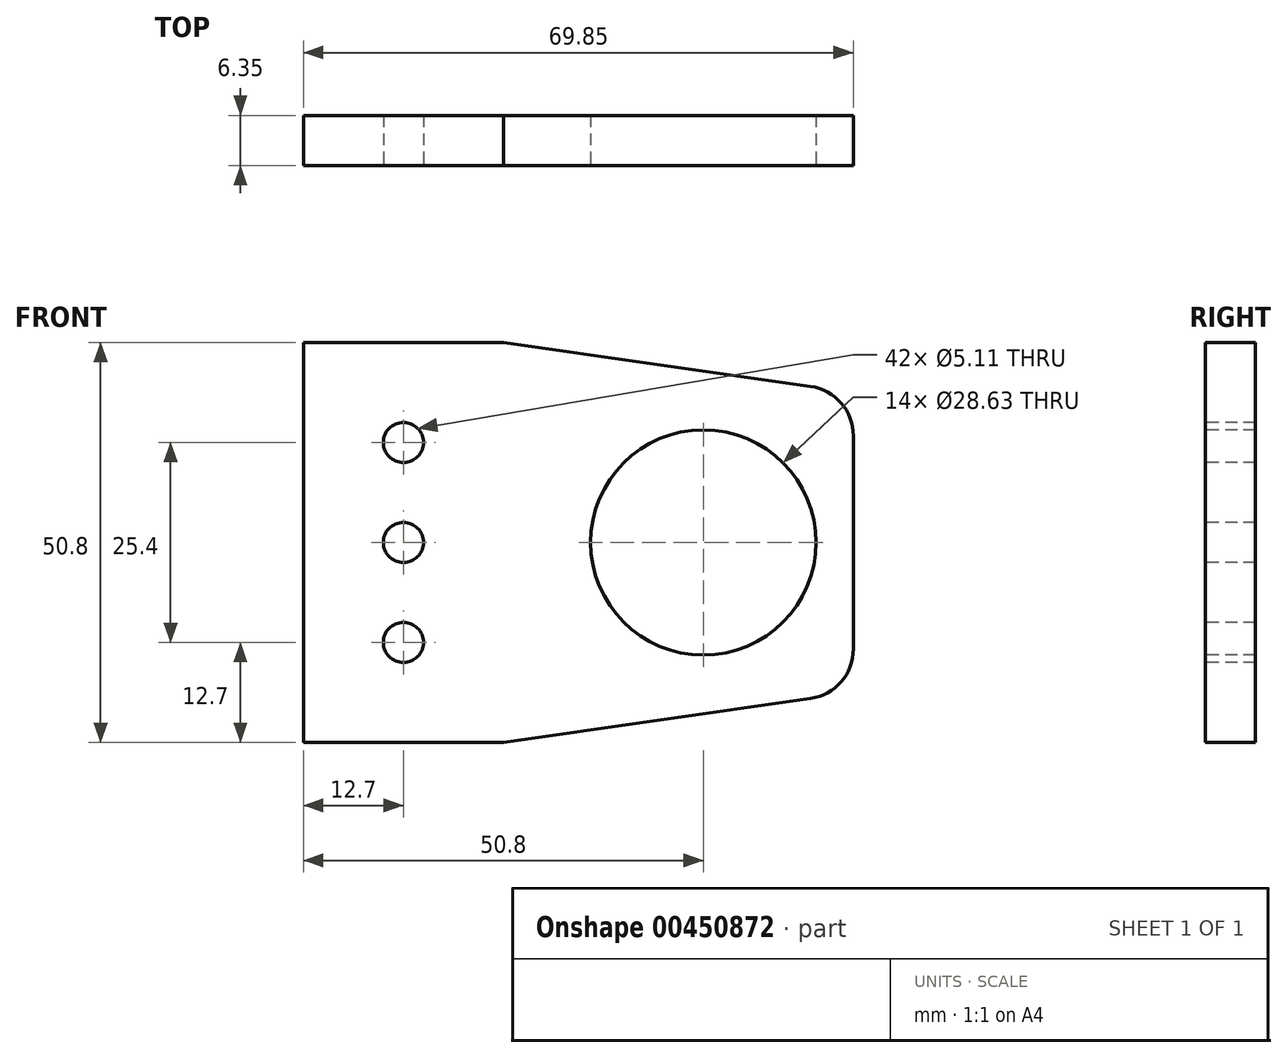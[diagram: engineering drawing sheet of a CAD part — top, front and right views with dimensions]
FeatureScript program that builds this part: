
annotation { "Feature Type Name" : "Feature", "Feature Type Description" : "" }
export const myFeature = defineFeature(function(context is Context, id is Id, definition is map)
    precondition{}
    {
        {
            var Q0;
            Q0=qCreatedBy(makeId("Front.planeOp"),FACE);
            var sketch = newSketch(context, id + "F0", { "sketchPlane" : qUnion([Q0])});
            skLineSegment(sketch, "E0.bottom", {"start": v(0, 25.4) * mm, "end": v(-25.4, 25.4) * mm});
            skLineSegment(sketch, "E0.top", {"start": v(0, -25.4) * mm, "end": v(-25.4, -25.4) * mm});
            skLineSegment(sketch, "E0.left", {"start": v(0, 25.4) * mm, "end": v(0, -25.4) * mm});
            skLineSegment(sketch, "E0.right", {"start": v(-25.4, 25.4) * mm, "end": v(-25.4, -25.4) * mm});
            skLineSegment(sketch, "E1", {"start": v(0, 0) * mm, "end": v(44.45, 0) * mm, "construction": true});
            skLineSegment(sketch, "E2", {"start": v(0, -25.4) * mm, "end": v(39, -19.83) * mm});
            skLineSegment(sketch, "E3", {"start": v(44.45, -13.54) * mm, "end": v(44.45, 0) * mm});
            skLineSegment(sketch, "E4.MirrorCS", {"start": v(0, 25.4) * mm, "end": v(39, 19.83) * mm});
            skLineSegment(sketch, "E5.MirrorCS", {"start": v(44.45, 13.54) * mm, "end": v(44.45, 0) * mm});
            skPoint(sketch, "E6.visualSharp", {"position": v(44.45, -19.05) * mm});
            skArc(sketch, "E6.filletArc", {"start": v(39, -19.83) * mm, "mid": v(42.9, -17.7) * mm, "end": v(44.45, -13.54) * mm});
            skPoint(sketch, "E7.visualSharp", {"position": v(44.45, 19.05) * mm});
            skArc(sketch, "E7.filletArc", {"start": v(44.45, 13.54) * mm, "mid": v(42.9, 17.7) * mm, "end": v(39, 19.83) * mm});
            skSolve(sketch);
        }
        {
            var Q0;
            Q0=qSketchRegion(id+"F0",true);
            extrude(context, id + "F1", {"entities" : qUnion([Q0]), "depth" : 6.35 * mm});
        }
        {
            var Q0;
            Q0=makeQuery(id+"F1.opExtrude","CAP_FACE",FACE,{"disambiguationData":[OSD([sQuery(id+"F0.wireOp",EDGE,"E0.bottom"),sQuery(id+"F0.wireOp",EDGE,"E0.top"),sQuery(id+"F0.wireOp",EDGE,"E0.right"),sQuery(id+"F0.wireOp",EDGE,"E2"),sQuery(id+"F0.wireOp",EDGE,"E3"),sQuery(id+"F0.wireOp",EDGE,"E4.MirrorCS"),sQuery(id+"F0.wireOp",EDGE,"E5.MirrorCS"),sQuery(id+"F0.wireOp",EDGE,"E6.filletArc"),sQuery(id+"F0.wireOp",EDGE,"E7.filletArc")])],"isStart":false});
            var sketch = newSketch(context, id + "F2", { "sketchPlane" : qUnion([Q0])});
            skLineSegment(sketch, "E8", {"start": v(-12.7, 25.4) * mm, "end": v(-12.7, -25.4) * mm, "construction": true});
            skPoint(sketch, "E9", {"position": v(-12.7, 12.7) * mm});
            skPoint(sketch, "E10", {"position": v(-12.7, 0) * mm});
            skPoint(sketch, "E11", {"position": v(-12.7, -12.7) * mm});
            skSolve(sketch);
        }
        {
            var Q0;
            Q0=sQuery(id+"F2.wireOp",VERTEX,"E9");
            var Q1;
            Q1=sQuery(id+"F2.wireOp",VERTEX,"E10");
            var Q2;
            Q2=sQuery(id+"F2.wireOp",VERTEX,"E11");
            var Q3;
            Q3=makeQuery(id+"F1.opExtrude","SWEPT_BODY",BODY,{"disambiguationData":[OSD([sQuery(id+"F0.wireOp",EDGE,"E0.bottom"),sQuery(id+"F0.wireOp",EDGE,"E0.top"),sQuery(id+"F0.wireOp",EDGE,"E0.right"),sQuery(id+"F0.wireOp",EDGE,"E2"),sQuery(id+"F0.wireOp",EDGE,"E3"),sQuery(id+"F0.wireOp",EDGE,"E4.MirrorCS"),sQuery(id+"F0.wireOp",EDGE,"E5.MirrorCS"),sQuery(id+"F0.wireOp",EDGE,"E6.filletArc"),sQuery(id+"F0.wireOp",EDGE,"E7.filletArc")])]});
            hole(context, id + "F3", {"style" : HoleStyle.SIMPLE, "endStyle" : HoleEndStyle.BLIND, "standardTappedOrClearance" : lookupTablePath({ "standard" : "ANSI", "fit" : "Normal (ASME)", "size" : "#10", "type" : "Clearance" }), "standardBlindInLast" : lookupTablePath({ "fit" : "Free", "standard" : "ANSI", "size" : "#10", "type" : "Clearance" }), "holeDiameter" : 5.1 * mm, "holeDepth" : 12.7 * mm, "isTappedThrough" : true, "tappedDepth" : 12.7 * mm, "tapClearance" : 3, "locations" : qUnion([Q0, Q1, Q2]), "scope" : qUnion([Q3])});
        }
        {
            var Q0;
            Q0=makeQuery(id+"F1.opExtrude","CAP_FACE",FACE,{"disambiguationData":[OSD([sQuery(id+"F0.wireOp",EDGE,"E0.bottom"),sQuery(id+"F0.wireOp",EDGE,"E0.top"),sQuery(id+"F0.wireOp",EDGE,"E0.right"),sQuery(id+"F0.wireOp",EDGE,"E2"),sQuery(id+"F0.wireOp",EDGE,"E3"),sQuery(id+"F0.wireOp",EDGE,"E4.MirrorCS"),sQuery(id+"F0.wireOp",EDGE,"E5.MirrorCS"),sQuery(id+"F0.wireOp",EDGE,"E6.filletArc"),sQuery(id+"F0.wireOp",EDGE,"E7.filletArc")])],"isStart":false});
            var sketch = newSketch(context, id + "F4", { "sketchPlane" : qUnion([Q0])});
            skCircle(sketch, "E12", {"center": v(25.4, 0) * mm, "radius": 14.31 * mm});
            skSolve(sketch);
        }
        {
            var Q0;
            Q0=qSketchRegion(id+"F4",true);
            extrude(context, id + "F5", {"entities" : qUnion([Q0]), "operationType" : NewBodyOperationType.REMOVE, "endBound" : BoundingType.UP_TO_NEXT, "oppositeDirection" : true, "depth" : 25.4 * mm});
        }
    });
